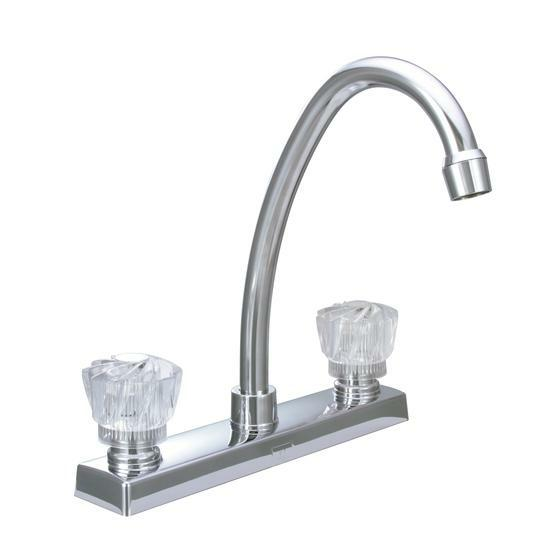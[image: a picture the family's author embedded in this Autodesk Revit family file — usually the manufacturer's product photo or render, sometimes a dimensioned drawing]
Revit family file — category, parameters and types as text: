
# Revit family: 01-1138-00 MEZCLADOR LAVAPLATOS 8” KRISTHAL
name_source: partatom
category: Plumbing Fixtures
revit_build: Autodesk Revit 2018 (Build: 20170223_1515(x64)
units: mm (PartAtom-declared; Revit-internal decimal feet)

## family parameters
Cut with Voids When Loaded = No
Host = Face
OmniClass Number = 23.31.11.00
Part Type = Normal
Room Calculation Point = No
Round Connector Dimension = Use Diameter
Shared = No

## types (1)
- 01-1138-00
    Alto = 265 mm
    Alto Aireador = 194.4 mm
    CW Connection = Yes
    Default Elevation = 0 mm  [stored 0 ft]
    Description = Bimando baño
    Eje (Roscas) = 203.2 mm  [stored 0.666667 ft]
    Eje - Aireador = 164.4 mm
    HW Connection = Yes
    Link Ficha Tecnica = https://infotecnica.gricol.com
    Manufacturer = Gricol
    Model = 01-1138-00
    Plastico ABS Cromado = Plastico - ABS Cromado
    Plastico Acrilico = Plastico Acrilico Transparente
    Product Name = MEZCLADOR LAVAPLATOS 8” KRISTHAL
    Type Image = MEZCLADOR LAVAPLATOS 8” KRISTHAL.jpg
    URL = https://www.gricol.com
    Vent Connection = No
    Waste Connection = No

note: [stored X ft] marks values corroborated as IEEE doubles in the binary element streams (Revit-internal decimal feet)

## geometry (parser evidence)
native form markers: Blend x2, Sweep x2
no freeform markers — native parametric forms only
